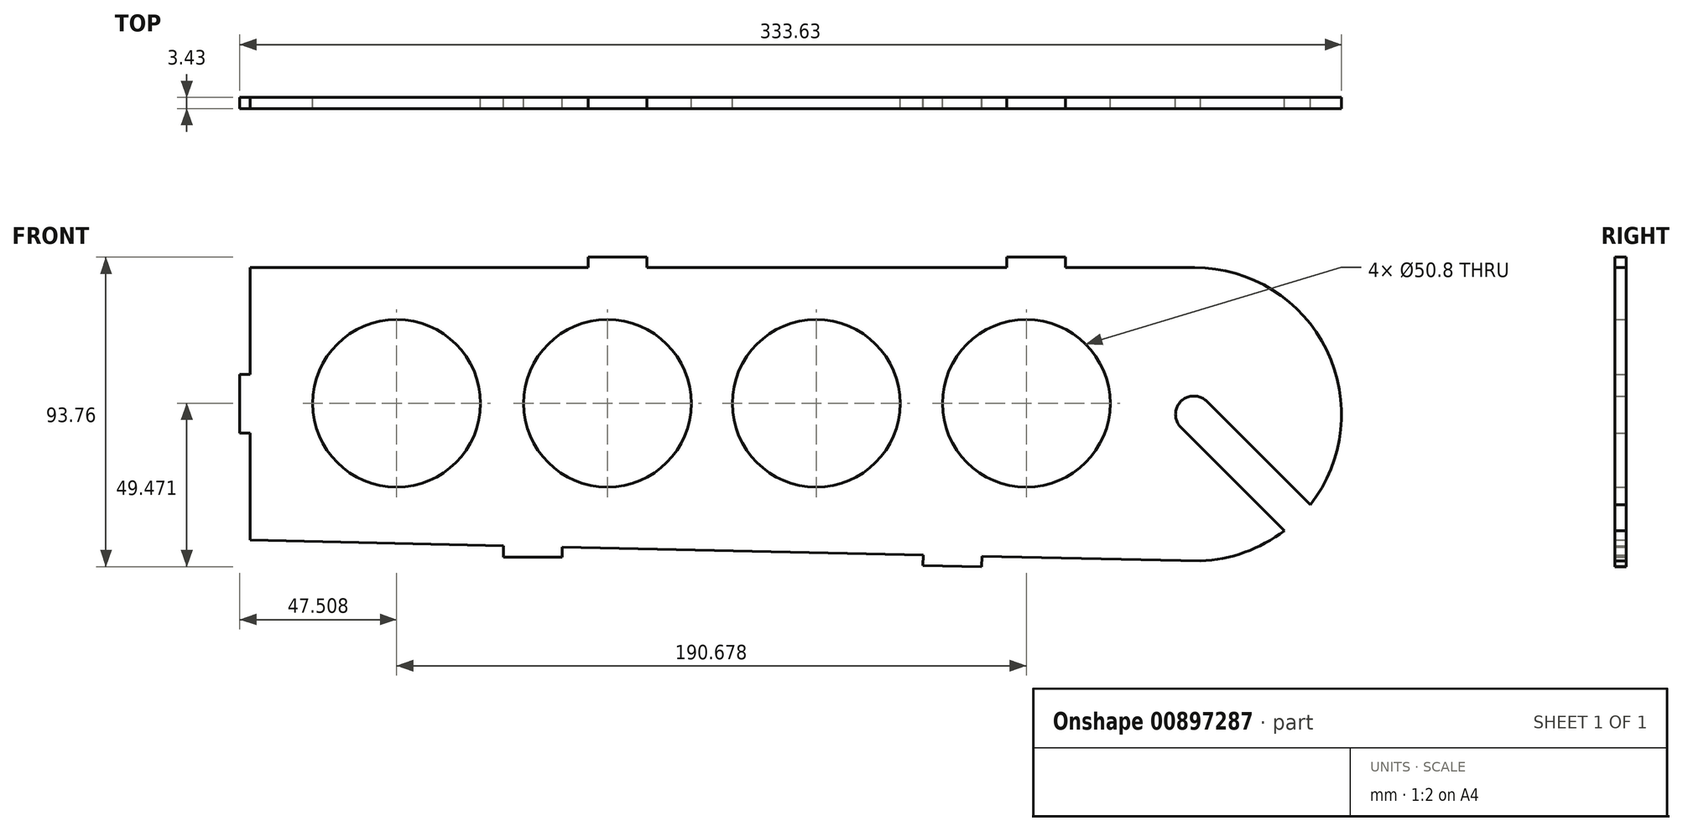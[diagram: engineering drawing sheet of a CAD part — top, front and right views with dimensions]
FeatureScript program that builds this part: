
annotation { "Feature Type Name" : "Feature", "Feature Type Description" : "" }
export const myFeature = defineFeature(function(context is Context, id is Id, definition is map)
    precondition{}
    {
        {
            var Q0;
            Q0=qCreatedBy(makeId("Front.planeOp"),FACE);
            var sketch = newSketch(context, id + "F0", { "sketchPlane" : qUnion([Q0])});
            skArc(sketch, "E0", {"start": v(49.65, 185.89) * mm, "mid": v(41.79, 185.89) * mm, "end": v(41.79, 178.03) * mm});
            skLineSegment(sketch, "E1", {"start": v(41.79, 178.03) * mm, "end": v(73.08, 146.73) * mm});
            skArc(sketch, "E2", {"start": v(47.68, 137.54) * mm, "mid": v(61.1, 140.16) * mm, "end": v(73.08, 146.73) * mm});
            skLineSegment(sketch, "E3", {"start": v(-18.54, 135.82) * mm, "end": v(-18.47, 139) * mm});
            skLineSegment(sketch, "E4", {"start": v(-36.32, 136.2) * mm, "end": v(-18.54, 135.82) * mm});
            skLineSegment(sketch, "E5", {"start": v(-36.25, 139.38) * mm, "end": v(-36.32, 136.2) * mm});
            skLineSegment(sketch, "E6", {"start": v(-145.54, 141.78) * mm, "end": v(-36.25, 139.38) * mm});
            skLineSegment(sketch, "E7", {"start": v(-145.54, 138.72) * mm, "end": v(-145.54, 141.78) * mm});
            skLineSegment(sketch, "E8", {"start": v(-163.32, 138.72) * mm, "end": v(-145.54, 138.72) * mm});
            skLineSegment(sketch, "E9", {"start": v(-163.32, 142.17) * mm, "end": v(-163.32, 138.72) * mm});
            skLineSegment(sketch, "E10", {"start": v(-240.03, 176.24) * mm, "end": v(-240.03, 143.86) * mm});
            skLineSegment(sketch, "E11", {"start": v(-243.2, 176.24) * mm, "end": v(-240.03, 176.24) * mm});
            skLineSegment(sketch, "E12", {"start": v(-243.2, 194.02) * mm, "end": v(-243.2, 176.24) * mm});
            skLineSegment(sketch, "E13", {"start": v(-240.03, 194.02) * mm, "end": v(-243.2, 194.02) * mm});
            skLineSegment(sketch, "E14", {"start": v(-240.03, 226.4) * mm, "end": v(-240.03, 194.02) * mm});
            skLineSegment(sketch, "E15", {"start": v(-137.64, 226.4) * mm, "end": v(-240.03, 226.4) * mm});
            skLineSegment(sketch, "E16", {"start": v(-137.64, 229.58) * mm, "end": v(-137.64, 226.4) * mm});
            skLineSegment(sketch, "E17", {"start": v(-119.86, 229.58) * mm, "end": v(-137.64, 229.58) * mm});
            skLineSegment(sketch, "E18", {"start": v(-119.86, 226.4) * mm, "end": v(-119.86, 229.58) * mm});
            skLineSegment(sketch, "E19", {"start": v(-10.9, 226.4) * mm, "end": v(-119.86, 226.4) * mm});
            skLineSegment(sketch, "E20", {"start": v(-10.9, 229.58) * mm, "end": v(-10.9, 226.4) * mm});
            skLineSegment(sketch, "E21", {"start": v(6.89, 229.58) * mm, "end": v(-10.9, 229.58) * mm});
            skLineSegment(sketch, "E22", {"start": v(6.89, 226.4) * mm, "end": v(6.89, 229.58) * mm});
            skLineSegment(sketch, "E23", {"start": v(45.97, 226.4) * mm, "end": v(6.89, 226.4) * mm});
            skLineSegment(sketch, "E24", {"start": v(80.97, 154.56) * mm, "end": v(49.65, 185.89) * mm});
            skCircle(sketch, "E25", {"center": v(-195.7, 185.3) * mm, "radius": 25.4 * mm});
            skCircle(sketch, "E26", {"center": v(-131.86, 185.3) * mm, "radius": 25.4 * mm});
            skCircle(sketch, "E27", {"center": v(-68.64, 185.3) * mm, "radius": 25.4 * mm});
            skCircle(sketch, "E28", {"center": v(-5.02, 185.3) * mm, "radius": 25.4 * mm});
            skLineSegment(sketch, "E29", {"start": v(-240.03, 143.86) * mm, "end": v(-163.32, 142.17) * mm});
            skLineSegment(sketch, "E30", {"start": v(-18.47, 139) * mm, "end": v(47.68, 137.54) * mm});
            skArc(sketch, "E31", {"start": v(80.97, 154.56) * mm, "mid": v(85.93, 201.42) * mm, "end": v(45.97, 226.4) * mm});
            skSolve(sketch);
        }
        {
            var Q0;
            Q0 = qSketchRegion(id + "F0", true);
            extrude(context, id + "F1", {"entities" : qUnion([Q0]), "depth" : 3.43 * mm, "offsetDistance" : 25.4 * mm});
        }
    });
